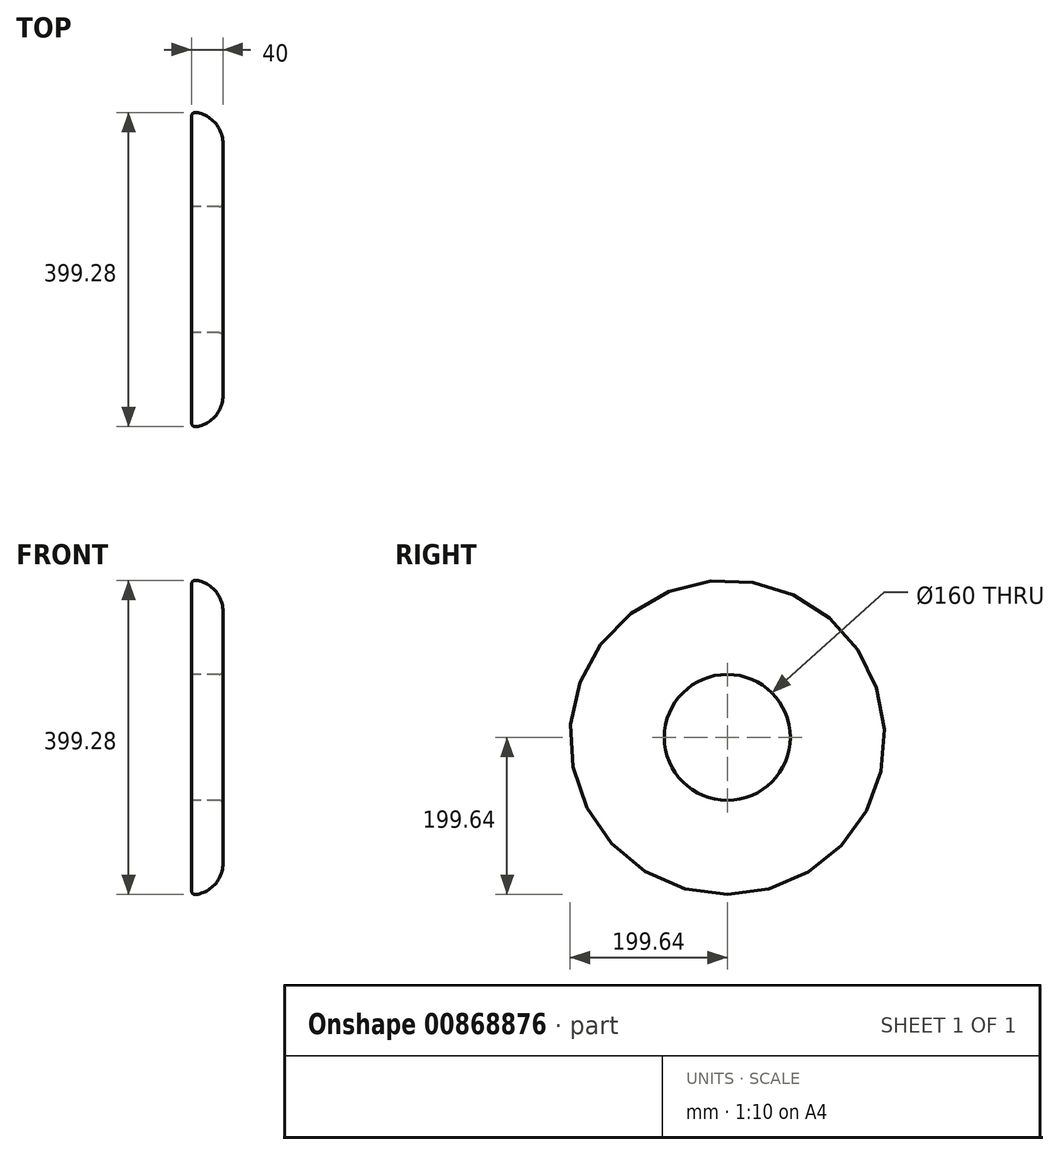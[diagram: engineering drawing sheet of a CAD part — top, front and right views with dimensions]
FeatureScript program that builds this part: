
annotation { "Feature Type Name" : "Feature", "Feature Type Description" : "" }
export const myFeature = defineFeature(function(context is Context, id is Id, definition is map)
    precondition{}
    {
        {
            var Q0;
            Q0=qCreatedBy(makeId("Front.planeOp"),FACE);
            var sketch = newSketch(context, id + "F0", { "sketchPlane" : qUnion([Q0])});
            skLineSegment(sketch, "E0.top", {"start": v(-20, -40) * mm, "end": v(20, -40) * mm});
            skLineSegment(sketch, "E0.left", {"start": v(-20, 40) * mm, "end": v(-20, -40) * mm});
            skLineSegment(sketch, "E0.right", {"start": v(20, 40) * mm, "end": v(20, -40) * mm});
            skPoint(sketch, "E0.middle", {"position": v(0, 0) * mm});
            skArc(sketch, "E1", {"start": v(20, 40) * mm, "mid": v(8.28, 68.28) * mm, "end": v(-20, 80) * mm});
            skLineSegment(sketch, "E2", {"start": v(-20, 40) * mm, "end": v(-20, 80) * mm});
            skLineSegment(sketch, "E3", {"start": v(-92.91, -120) * mm, "end": v(123.53, -120) * mm});
            skSolve(sketch);
        }
        {
            var Q0;
            Q0=makeQuery(id+"F0.imprint","IMPRINT",FACE,{"disambiguationData":[TD([[makeQuery(id+"F0.imprint","IMPRINT",EDGE,{"derivedFrom":sQuery(id+"F0.wireOp",EDGE,"E0.top")}),1.0]])]});
            var Q1;
            Q1=sQuery(id+"F0.wireOp",EDGE,"E3");
            revolve(context, id + "F1", {"surfaceOperationType" : NewSurfaceOperationType.NEW, "entities" : qUnion([Q0]), "axis" : qUnion([Q1]), "revolveType" : RevolveType.FULL});
        }
        {
            var Q0;
            Q0=makeQuery(id+"F1.opRevolve","SWEPT_EDGE",EDGE,{"disambiguationData":[OSD([sQuery(id+"F0.wireOp",EDGE,"E1"),sQuery(id+"F0.wireOp",EDGE,"E2")])]});
            fillet(context, id + "F2", {"entities" : qUnion([Q0]), "radius" : 5 * mm, "tangentPropagation" : true, "allowEdgeOverflow" : false});
        }
        {
            var Q0;
            Q0=makeQuery(id+"F1.opRevolve","SWEPT_EDGE",EDGE,{"disambiguationData":[OSD([sQuery(id+"F0.wireOp",EDGE,"E0.top"),sQuery(id+"F0.wireOp",EDGE,"E0.right")])]});
            fillet(context, id + "F3", {"entities" : qUnion([Q0]), "radius" : 5 * mm, "tangentPropagation" : true, "allowEdgeOverflow" : false});
        }
    });
